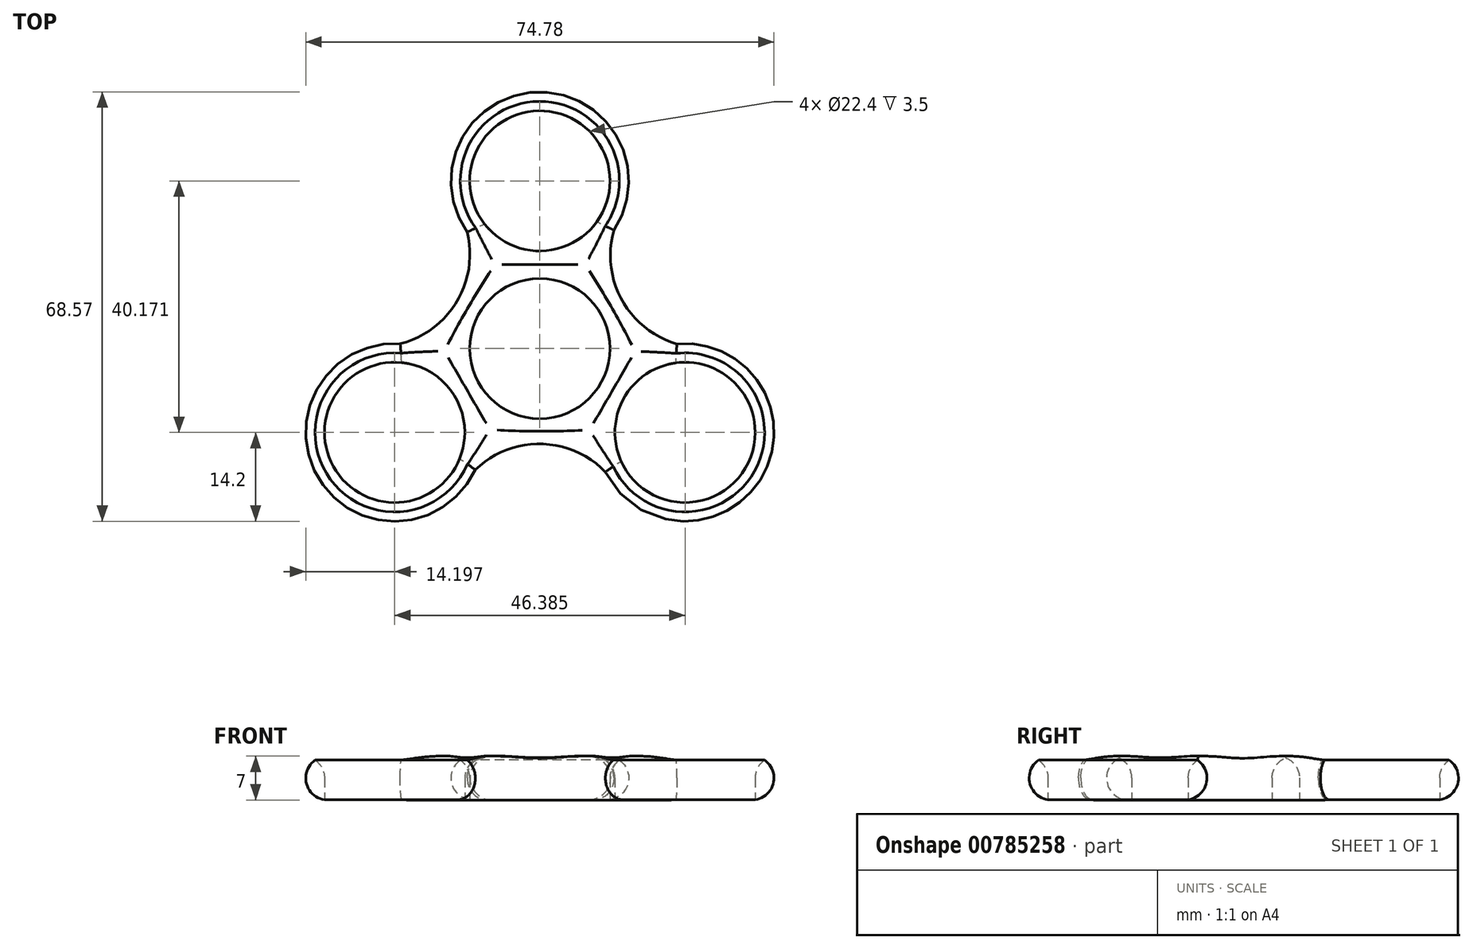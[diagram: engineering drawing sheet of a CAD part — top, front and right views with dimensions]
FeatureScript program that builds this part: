
annotation { "Feature Type Name" : "Feature", "Feature Type Description" : "" }
export const myFeature = defineFeature(function(context is Context, id is Id, definition is map)
    precondition{}
    {
        {
            var Q0;
            Q0=qCreatedBy(makeId("Top.planeOp"),FACE);
            var sketch = newSketch(context, id + "F0", { "sketchPlane" : qUnion([Q0])});
            skCircle(sketch, "E0", {"center": v(0, 0) * mm, "radius": 11.2 * mm});
            skCircle(sketch, "E1", {"center": v(0, 26.78) * mm, "radius": 11.2 * mm});
            skArc(sketch, "E2", {"start": v(11.83, 18.92) * mm, "mid": v(-0.2, 40.98) * mm, "end": v(-11.6, 18.6) * mm});
            skCircle(sketch, "E3.1.0", {"center": v(-23.2, -13.4) * mm, "radius": 11.2 * mm});
            skArc(sketch, "E3.1.1", {"start": v(-22.3, 0.78) * mm, "mid": v(-35.39, -20.66) * mm, "end": v(-10.3, -19.35) * mm});
            skCircle(sketch, "E3.2.0", {"center": v(23.2, -13.4) * mm, "radius": 11.2 * mm});
            skArc(sketch, "E3.2.1", {"start": v(10.47, -19.7) * mm, "mid": v(35.59, -20.32) * mm, "end": v(21.9, 0.75) * mm});
            skArc(sketch, "E4", {"start": v(11.83, 18.92) * mm, "mid": v(13.1, 7.75) * mm, "end": v(21.9, 0.75) * mm});
            skArc(sketch, "E5.1.0", {"start": v(-22.3, 0.78) * mm, "mid": v(-13.27, 7.47) * mm, "end": v(-11.6, 18.6) * mm});
            skArc(sketch, "E5.2.0", {"start": v(10.47, -19.7) * mm, "mid": v(0.16, -15.23) * mm, "end": v(-10.3, -19.35) * mm});
            skLineSegment(sketch, "E6.trimOffspring", {"start": v(11.04, 6.29) * mm, "end": v(11.63, 6.63) * mm});
            skSolve(sketch);
        }
        {
            var Q0;
            Q0=makeQuery(id+"F0.imprint","IMPRINT",FACE,{"disambiguationData":[TD([[makeQuery(id+"F0.imprint","IMPRINT",EDGE,{"derivedFrom":sQuery(id+"F0.wireOp",EDGE,"E0")}),-1.0]])]});
            extrude(context, id + "F1", {"entities" : qUnion([Q0]), "depth" : 7 * mm, "offsetDistance" : 25 * mm});
        }
        {
            var Q0;
            Q0=makeQuery(id+"F1.opExtrude","CAP_EDGE",EDGE,{"disambiguationData":[OSD([sQuery(id+"F0.wireOp",EDGE,"E5.1.0")])],"isStart":false});
            var Q1;
            Q1=makeQuery(id+"F1.opExtrude","CAP_EDGE",EDGE,{"disambiguationData":[OSD([sQuery(id+"F0.wireOp",EDGE,"E2")])],"isStart":false});
            var Q2;
            Q2=makeQuery(id+"F1.opExtrude","CAP_EDGE",EDGE,{"disambiguationData":[OSD([sQuery(id+"F0.wireOp",EDGE,"E4")])],"isStart":false});
            var Q3;
            Q3=makeQuery(id+"F1.opExtrude","CAP_EDGE",EDGE,{"disambiguationData":[OSD([sQuery(id+"F0.wireOp",EDGE,"E3.2.1")])],"isStart":false});
            var Q4;
            Q4=makeQuery(id+"F1.opExtrude","CAP_FACE",FACE,{"disambiguationData":[OSD([sQuery(id+"F0.wireOp",EDGE,"E0"),sQuery(id+"F0.wireOp",EDGE,"E1"),sQuery(id+"F0.wireOp",EDGE,"E2"),sQuery(id+"F0.wireOp",EDGE,"E3.1.0"),sQuery(id+"F0.wireOp",EDGE,"E3.1.1"),sQuery(id+"F0.wireOp",EDGE,"E3.2.0"),sQuery(id+"F0.wireOp",EDGE,"E3.2.1"),sQuery(id+"F0.wireOp",EDGE,"E4"),sQuery(id+"F0.wireOp",EDGE,"E5.1.0"),sQuery(id+"F0.wireOp",EDGE,"E5.2.0")])],"isStart":false});
            fillet(context, id + "F2", {"entities" : qUnion([Q0, Q1, Q2, Q3, Q4]), "radius" : 3.5 * mm, "tangentPropagation" : true, "allowEdgeOverflow" : false});
        }
        {
            var Q0;
            Q0=makeQuery(id+"F1.opExtrude","CAP_EDGE",EDGE,{"disambiguationData":[OSD([sQuery(id+"F0.wireOp",EDGE,"E3.1.1")])],"isStart":true});
            var Q1;
            Q1=makeQuery(id+"F1.opExtrude","CAP_EDGE",EDGE,{"disambiguationData":[OSD([sQuery(id+"F0.wireOp",EDGE,"E5.2.0")])],"isStart":true});
            var Q2;
            Q2=makeQuery(id+"F1.opExtrude","CAP_EDGE",EDGE,{"disambiguationData":[OSD([sQuery(id+"F0.wireOp",EDGE,"E3.2.1")])],"isStart":true});
            var Q3;
            Q3=makeQuery(id+"F1.opExtrude","CAP_EDGE",EDGE,{"disambiguationData":[OSD([sQuery(id+"F0.wireOp",EDGE,"E4")])],"isStart":true});
            var Q4;
            Q4=makeQuery(id+"F1.opExtrude","CAP_EDGE",EDGE,{"disambiguationData":[OSD([sQuery(id+"F0.wireOp",EDGE,"E2")])],"isStart":true});
            var Q5;
            Q5=makeQuery(id+"F1.opExtrude","CAP_EDGE",EDGE,{"disambiguationData":[OSD([sQuery(id+"F0.wireOp",EDGE,"E5.1.0")])],"isStart":true});
            fillet(context, id + "F3", {"entities" : qUnion([Q0, Q1, Q2, Q3, Q4, Q5]), "radius" : 3.5 * mm, "tangentPropagation" : true, "allowEdgeOverflow" : false});
        }
    });
